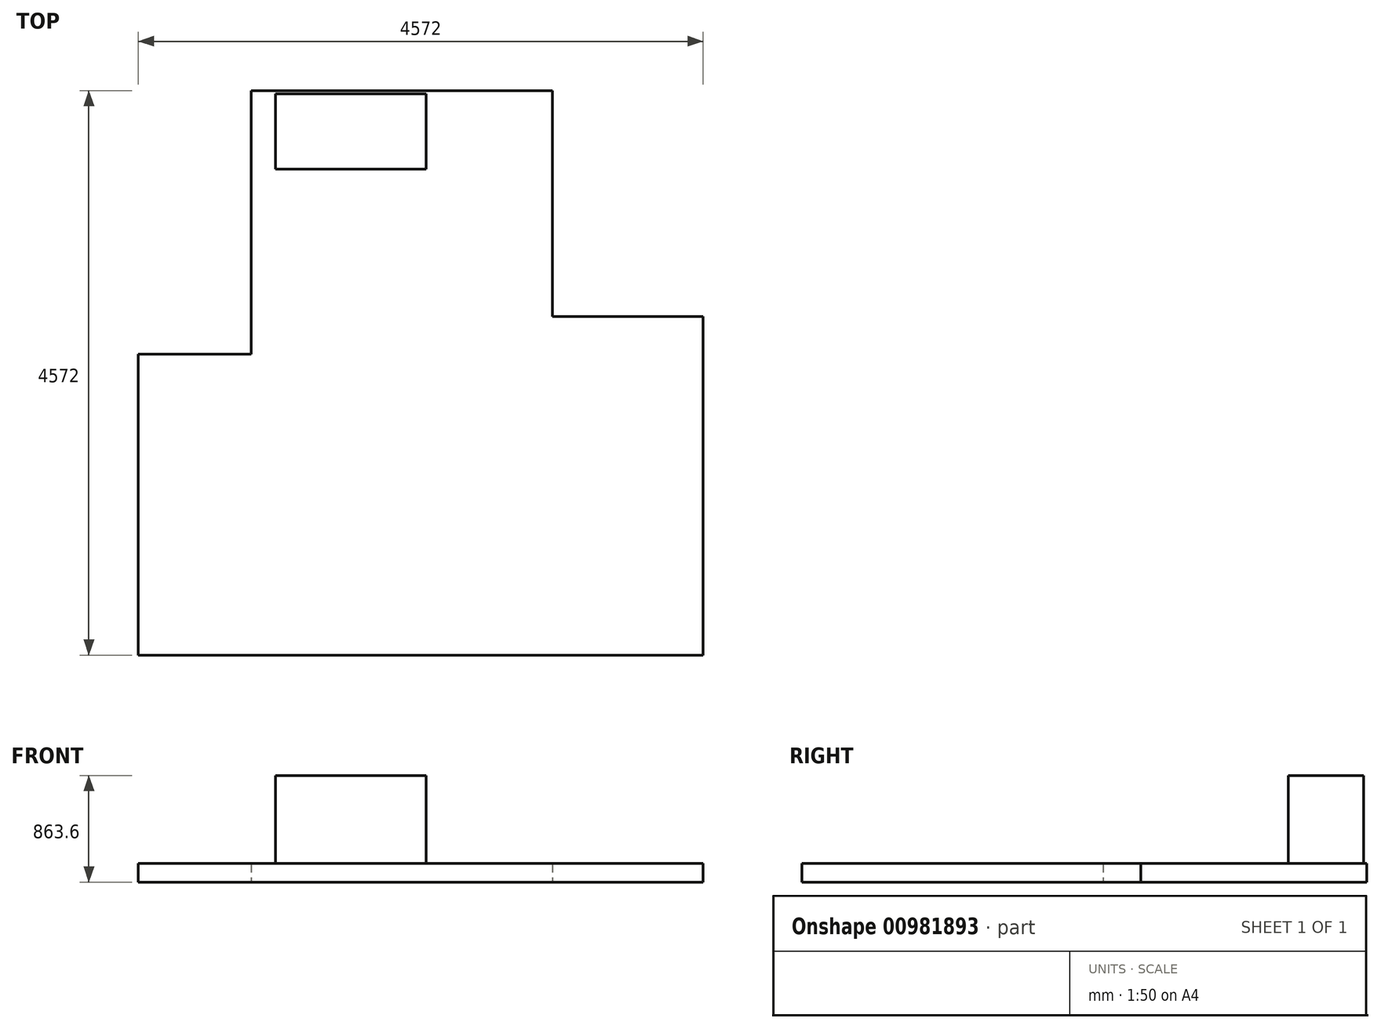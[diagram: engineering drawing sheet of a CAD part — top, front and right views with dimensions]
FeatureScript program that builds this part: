
annotation { "Feature Type Name" : "Feature", "Feature Type Description" : "" }
export const myFeature = defineFeature(function(context is Context, id is Id, definition is map)
    precondition{}
    {
        {
            var Q0;
            Q0=qCreatedBy(makeId("Top.planeOp"),FACE);
            var sketch = newSketch(context, id + "F0", { "sketchPlane" : qUnion([Q0])});
            skLineSegment(sketch, "E0", {"start": v(240.62, 4695.04) * mm, "end": v(2679.02, 4695.04) * mm});
            skLineSegment(sketch, "E1", {"start": v(2679.02, 4695.04) * mm, "end": v(2679.02, 2866.24) * mm});
            skLineSegment(sketch, "E2", {"start": v(2679.02, 2866.24) * mm, "end": v(3898.22, 2866.24) * mm});
            skLineSegment(sketch, "E3", {"start": v(3898.22, 2866.24) * mm, "end": v(3898.22, 123.04) * mm});
            skLineSegment(sketch, "E4", {"start": v(3898.22, 123.04) * mm, "end": v(-673.78, 123.04) * mm});
            skLineSegment(sketch, "E5", {"start": v(-673.78, 123.04) * mm, "end": v(-673.78, 2561.44) * mm});
            skLineSegment(sketch, "E6", {"start": v(-673.78, 2561.44) * mm, "end": v(240.62, 2561.44) * mm});
            skLineSegment(sketch, "E7", {"start": v(240.62, 2561.44) * mm, "end": v(240.62, 4695.04) * mm});
            skSolve(sketch);
        }
        {
            var Q0;
            Q0 = qSketchRegion(id + "F0", true);
            extrude(context, id + "F1", {"entities" : qUnion([Q0]), "depth" : 152.4 * mm, "offsetDistance" : 25.4 * mm});
        }
        {
            var Q0;
            Q0=makeQuery(id+"F1.opExtrude","CAP_FACE",FACE,{"disambiguationData":[OSD([sQuery(id+"F0.wireOp",EDGE,"E0"),sQuery(id+"F0.wireOp",EDGE,"E1"),sQuery(id+"F0.wireOp",EDGE,"E2"),sQuery(id+"F0.wireOp",EDGE,"E3"),sQuery(id+"F0.wireOp",EDGE,"E4"),sQuery(id+"F0.wireOp",EDGE,"E5"),sQuery(id+"F0.wireOp",EDGE,"E6"),sQuery(id+"F0.wireOp",EDGE,"E7")])],"isStart":false});
            var sketch = newSketch(context, id + "F2", { "sketchPlane" : qUnion([Q0])});
            skLineSegment(sketch, "E8", {"start": v(436.65, 4058.18) * mm, "end": v(436.65, 4667.78) * mm});
            skLineSegment(sketch, "E9", {"start": v(436.65, 4667.78) * mm, "end": v(1655.85, 4667.78) * mm});
            skLineSegment(sketch, "E10", {"start": v(1655.85, 4667.78) * mm, "end": v(1655.85, 4058.18) * mm});
            skLineSegment(sketch, "E11", {"start": v(1655.85, 4058.18) * mm, "end": v(436.65, 4058.18) * mm});
            skSolve(sketch);
        }
        {
            var Q0;
            Q0 = qSketchRegion(id + "F2", true);
            extrude(context, id + "F3", {"entities" : qUnion([Q0]), "operationType" : NewBodyOperationType.ADD, "depth" : 711.2 * mm, "offsetDistance" : 25.4 * mm});
        }
    });
